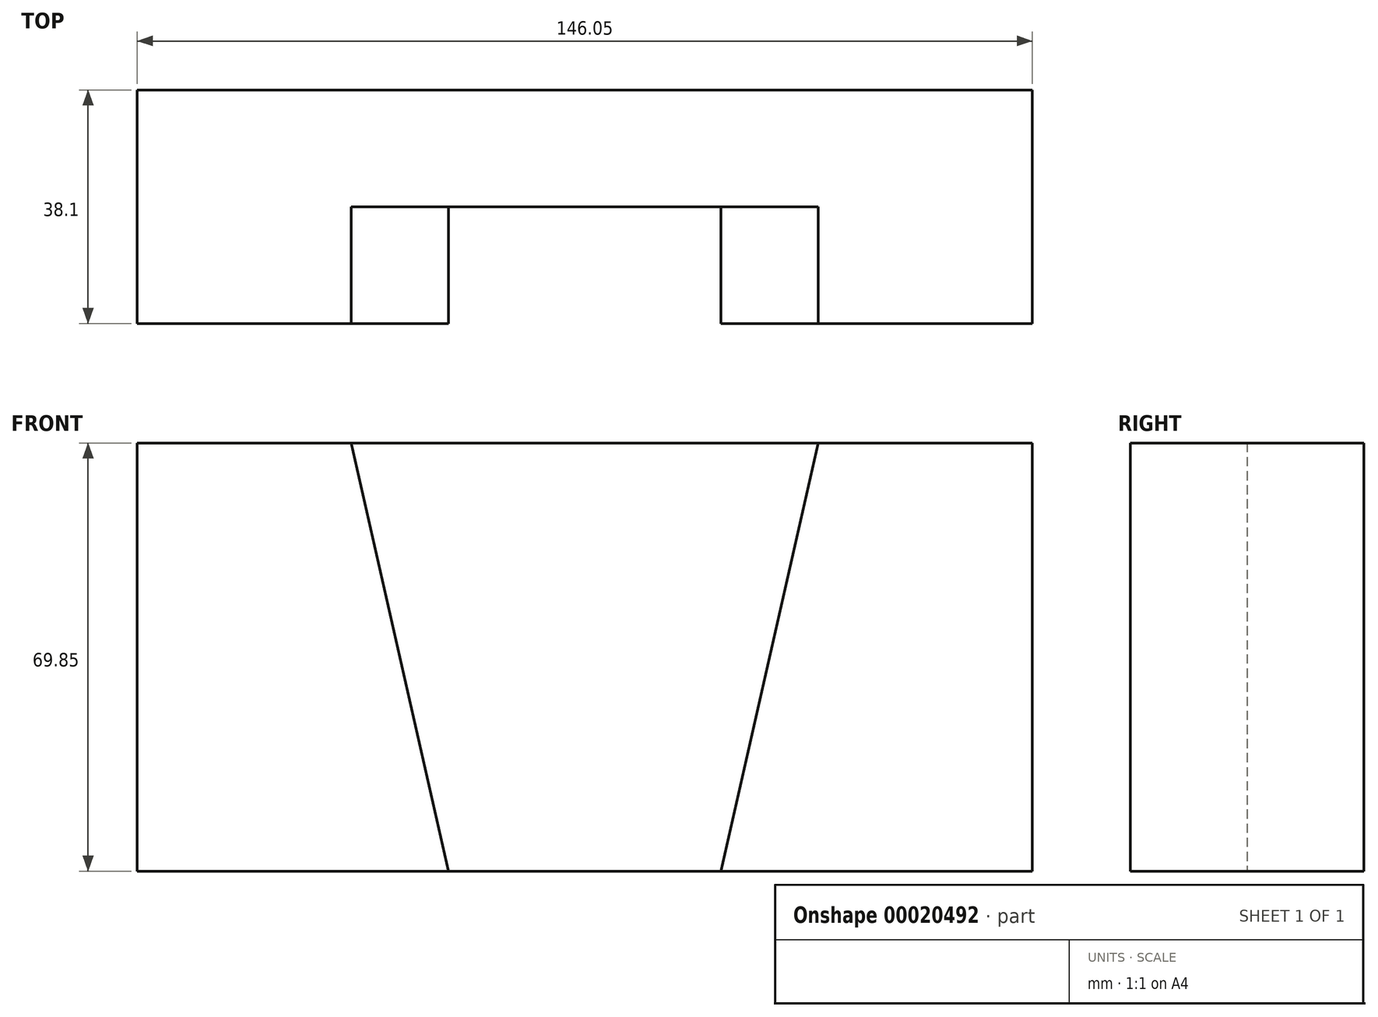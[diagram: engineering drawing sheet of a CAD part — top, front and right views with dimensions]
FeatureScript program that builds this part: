
annotation { "Feature Type Name" : "Feature", "Feature Type Description" : "" }
export const myFeature = defineFeature(function(context is Context, id is Id, definition is map)
    precondition{}
    {
        {
            var Q0;
            Q0=qCreatedBy(makeId("Front.planeOp"),FACE);
            var sketch = newSketch(context, id + "F0", { "sketchPlane" : qUnion([Q0])});
            skLineSegment(sketch, "E0.left", {"start": v(-57.88, 52.15) * mm, "end": v(-57.88, -17.7) * mm});
            skLineSegment(sketch, "E0.right", {"start": v(15.15, 52.15) * mm, "end": v(15.15, -17.7) * mm});
            skPoint(sketch, "E1", {"position": v(-7.08, -17.7) * mm});
            skLineSegment(sketch, "E2", {"start": v(-7.08, -17.7) * mm, "end": v(15.15, -17.7) * mm});
            skLineSegment(sketch, "E3", {"start": v(-57.88, 52.15) * mm, "end": v(-22.95, 52.15) * mm});
            skLineSegment(sketch, "E4", {"start": v(-22.95, 52.15) * mm, "end": v(-7.08, -17.7) * mm});
            skLineSegment(sketch, "E5", {"start": v(-22.95, 52.15) * mm, "end": v(15.15, 52.15) * mm});
            skLineSegment(sketch, "E6", {"start": v(-7.08, -17.7) * mm, "end": v(-57.88, -17.7) * mm});
            skSolve(sketch);
        }
        {
            var Q0;
            Q0=makeQuery(id+"F0.imprint","IMPRINT",FACE,{"disambiguationData":[TD([[makeQuery(id+"F0.imprint","IMPRINT",EDGE,{"derivedFrom":sQuery(id+"F0.wireOp",EDGE,"E0.left")}),1.0]])]});
            extrude(context, id + "F1", {"entities" : qUnion([Q0]), "depth" : 38.1 * mm});
        }
        {
            var Q0;
            Q0=makeQuery(id+"F0.imprint","IMPRINT",FACE,{"disambiguationData":[TD([[makeQuery(id+"F0.imprint","IMPRINT",EDGE,{"derivedFrom":sQuery(id+"F0.wireOp",EDGE,"E0.right")}),-1.0]])]});
            extrude(context, id + "F2", {"entities" : qUnion([Q0]), "operationType" : NewBodyOperationType.ADD, "depth" : 19.05 * mm});
        }
        {
            var Q0;
            Q0=makeQuery(id+"F1.opExtrude","SWEPT_BODY",BODY,{"disambiguationData":[OSD([sQuery(id+"F0.wireOp",EDGE,"E0.left"),sQuery(id+"F0.wireOp",EDGE,"E3"),sQuery(id+"F0.wireOp",EDGE,"E4"),sQuery(id+"F0.wireOp",EDGE,"E6")])]});
            var Q1;
            Q1=makeQuery(id+"F2.opExtrude","SWEPT_FACE",FACE,{"disambiguationData":[OSD([sQuery(id+"F0.wireOp",EDGE,"E0.right")])]});
            mirror(context, id + "F3", {"operationType" : NewBodyOperationType.ADD, "entities" : qUnion([Q0]), "mirrorPlane" : qUnion([Q1])});
        }
    });
